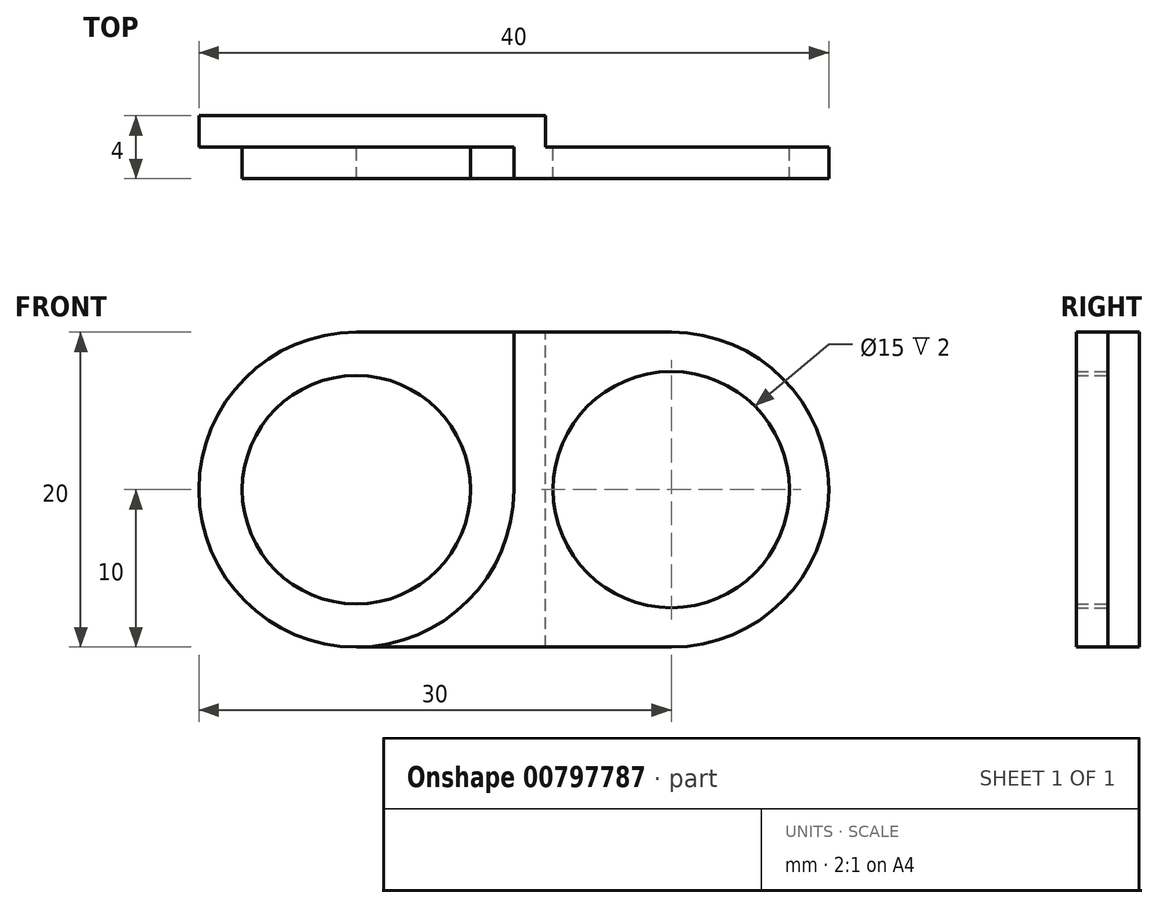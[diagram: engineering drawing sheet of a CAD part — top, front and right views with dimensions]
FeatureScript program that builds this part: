
annotation { "Feature Type Name" : "Feature", "Feature Type Description" : "" }
export const myFeature = defineFeature(function(context is Context, id is Id, definition is map)
    precondition{}
    {
        {
            var Q0;
            Q0=qCreatedBy(makeId("Front.planeOp"),FACE);
            var sketch = newSketch(context, id + "F0", { "sketchPlane" : qUnion([Q0])});
            skCircle(sketch, "E0", {"center": v(0, 0) * mm, "radius": 7.5 * mm});
            skCircle(sketch, "E1", {"center": v(-20, 0) * mm, "radius": 7.25 * mm});
            skLineSegment(sketch, "E2", {"start": v(-20, 0) * mm, "end": v(0, 0) * mm, "construction": true});
            skArc(sketch, "E3.0.startCap", {"start": v(-10, 0) * mm, "mid": v(-27.07, -7.07) * mm, "end": v(-20, 10) * mm});
            skArc(sketch, "E3.0.endCap", {"start": v(0, 10) * mm, "mid": v(10, 0) * mm, "end": v(0, -10) * mm});
            skLineSegment(sketch, "E3.0.left", {"start": v(-20, 10) * mm, "end": v(0, 10) * mm});
            skLineSegment(sketch, "E3.0.right", {"start": v(-20, -10) * mm, "end": v(0, -10) * mm});
            skLineSegment(sketch, "E4", {"start": v(-10, 0) * mm, "end": v(-10, 10) * mm});
            skLineSegment(sketch, "E5", {"start": v(-8, -10) * mm, "end": v(-8, 10) * mm});
            skSolve(sketch);
        }
        {
            var Q0;
            Q0=makeQuery(id+"F0.imprint","IMPRINT",FACE,{"disambiguationData":[TD([[makeQuery(id+"F0.imprint","IMPRINT",EDGE,{"derivedFrom":sQuery(id+"F0.wireOp",EDGE,"E0")}),-1.0]])]});
            var Q1;
            {var subQ0=sQuery(id+"F0.wireOp",EDGE,"E4");Q1=makeQuery(id+"F0.imprint","IMPRINT",FACE,{"disambiguationData":[TD([[makeQuery(id+"F0.imprint","IMPRINT",EDGE,{"derivedFrom":subQ0}),-1.0]])]});}
            extrude(context, id + "F1", {"entities" : qUnion([Q0, Q1]), "depth" : 2 * mm, "offsetDistance" : 25 * mm});
        }
        {
            var Q0;
            {var subQ0=sQuery(id+"F0.wireOp",EDGE,"E4");Q0=makeQuery(id+"F0.imprint","IMPRINT",FACE,{"disambiguationData":[TD([[makeQuery(id+"F0.imprint","IMPRINT",EDGE,{"derivedFrom":subQ0}),-1.0]])]});}
            var Q1;
            Q1=makeQuery(id+"F0.imprint","IMPRINT",FACE,{"disambiguationData":[TD([[makeQuery(id+"F0.imprint","IMPRINT",EDGE,{"derivedFrom":sQuery(id+"F0.wireOp",EDGE,"E1")}),-1.0]])]});
            extrude(context, id + "F2", {"entities" : qUnion([Q0, Q1]), "operationType" : NewBodyOperationType.ADD, "oppositeDirection" : true, "depth" : 2 * mm, "offsetDistance" : 25 * mm});
        }
        {
            var Q0;
            Q0=makeQuery(id+"F0.imprint","IMPRINT",FACE,{"disambiguationData":[TD([[makeQuery(id+"F0.imprint","IMPRINT",EDGE,{"derivedFrom":sQuery(id+"F0.wireOp",EDGE,"E1")}),1.0]])]});
            var Q1;
            Q1=makeQuery(id+"F1.opExtrude","CAP_FACE",FACE,{"disambiguationData":[OSD([sQuery(id+"F0.wireOp",EDGE,"E0"),sQuery(id+"F0.wireOp",EDGE,"E3.0.startCap"),sQuery(id+"F0.wireOp",EDGE,"E3.0.endCap"),sQuery(id+"F0.wireOp",EDGE,"E3.0.left"),sQuery(id+"F0.wireOp",EDGE,"E3.0.right"),sQuery(id+"F0.wireOp",EDGE,"E4")])],"isStart":false});
            var Q2;
            Q2=makeQuery(id+"F2.opExtrude","CAP_FACE",FACE,{"disambiguationData":[OSD([sQuery(id+"F0.wireOp",EDGE,"E1"),sQuery(id+"F0.wireOp",EDGE,"E3.0.startCap"),sQuery(id+"F0.wireOp",EDGE,"E3.0.left"),sQuery(id+"F0.wireOp",EDGE,"E3.0.right"),sQuery(id+"F0.wireOp",EDGE,"E5")])],"isStart":false});
            extrude(context, id + "F3", {"entities" : qUnion([Q0]), "operationType" : NewBodyOperationType.ADD, "endBound" : BoundingType.UP_TO_SURFACE, "depth" : 4 * mm, "endBoundEntityFace" : qUnion([Q1]), "offsetDistance" : 25 * mm, "hasSecondDirection" : true, "secondDirectionBound" : SecondDirectionBoundingType.UP_TO_SURFACE, "secondDirectionOppositeDirection" : true, "secondDirectionDepth" : 25 * mm, "secondDirectionBoundEntityFace" : qUnion([Q2])});
        }
    });
